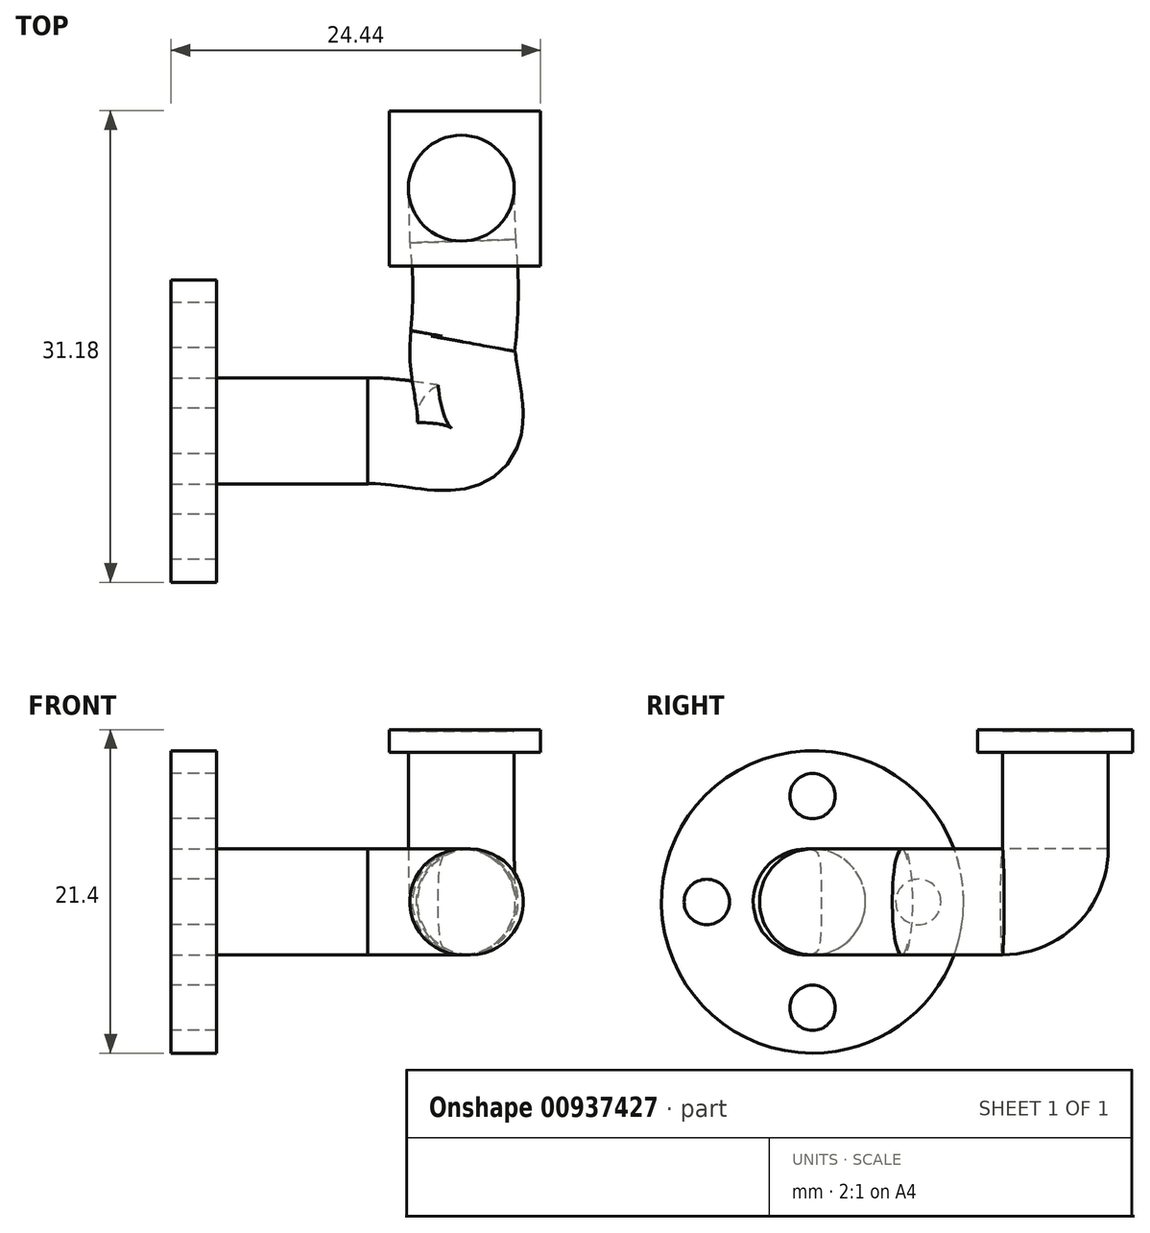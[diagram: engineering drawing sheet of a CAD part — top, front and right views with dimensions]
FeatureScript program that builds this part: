
annotation { "Feature Type Name" : "Feature", "Feature Type Description" : "" }
export const myFeature = defineFeature(function(context is Context, id is Id, definition is map)
    precondition{}
    {
        {
            var Q0;
            Q0=qCreatedBy(makeId("Right.planeOp"),FACE);
            var sketch = newSketch(context, id + "F0", { "sketchPlane" : qUnion([Q0])});
            skCircle(sketch, "E0", {"center": v(0, 7) * mm, "radius": 1.5 * mm});
            skCircle(sketch, "E1.1.0", {"center": v(-7, 0) * mm, "radius": 1.5 * mm});
            skCircle(sketch, "E1.2.0", {"center": v(0, -7) * mm, "radius": 1.5 * mm});
            skCircle(sketch, "E1.3.0", {"center": v(7, 0) * mm, "radius": 1.5 * mm});
            skPoint(sketch, "E1.center", {"position": v(0, 0) * mm});
            skCircle(sketch, "E2", {"center": v(0, 0) * mm, "radius": 10 * mm});
            skSolve(sketch);
        }
        {
            var Q0;
            Q0=qSketchRegion(id+"F0",true);
            extrude(context, id + "F1", {"entities" : qUnion([Q0]), "depth" : 3 * mm, "offsetDistance" : 25 * mm});
        }
        {
            var Q0;
            Q0=makeQuery(id+"F1.opExtrude","CAP_FACE",FACE,{"disambiguationData":[OSD([sQuery(id+"F0.wireOp",EDGE,"E0"),sQuery(id+"F0.wireOp",EDGE,"E1.1.0"),sQuery(id+"F0.wireOp",EDGE,"E1.2.0"),sQuery(id+"F0.wireOp",EDGE,"E1.3.0"),sQuery(id+"F0.wireOp",EDGE,"E2")])],"isStart":false});
            var sketch = newSketch(context, id + "F2", { "sketchPlane" : qUnion([Q0])});
            skCircle(sketch, "E3", {"center": v(0, 0) * mm, "radius": 3.5 * mm});
            skSolve(sketch);
        }
        {
            var Q0;
            Q0=qSketchRegion(id+"F2",true);
            extrude(context, id + "F3", {"entities" : qUnion([Q0]), "operationType" : NewBodyOperationType.ADD, "depth" : 10 * mm, "offsetDistance" : 25 * mm});
        }
        {
            var Q0;
            Q0=qSketchRegion(id+"F2",true);
            extrude(context, id + "F4", {"entities" : qUnion([Q0]), "operationType" : NewBodyOperationType.REMOVE, "endBound" : BoundingType.THROUGH_ALL, "oppositeDirection" : true, "depth" : 25 * mm, "offsetDistance" : 25 * mm});
        }
        {
            var Q0;
            Q0=qCreatedBy(makeId("Top.planeOp"),FACE);
            var sketch = newSketch(context, id + "F5", { "sketchPlane" : qUnion([Q0])});
            skFitSpline(sketch, "E4", {"points": [v(13.48, 0) * mm, v(19.49, 0) * mm, v(19.39, 6.5) * mm], "startDerivative": vector(13.33, 0) * mm, "endDerivative": vector(2.61, 14.76) * mm});
            skSolve(sketch);
        }
        {
            var Q0;
            Q0=makeQuery(id+"F3.opExtrude","CAP_FACE",FACE,{"disambiguationData":[OSD([sQuery(id+"F2.wireOp",EDGE,"E3")])],"isStart":false});
            var Q1;
            Q1=sQuery(id+"F5.wireOp",EDGE,"E4");
            sweep(context, id + "F6", {"operationType" : NewBodyOperationType.ADD, "profiles" : qUnion([Q0]), "path" : qUnion([Q1])});
        }
        {
            var Q0;
            Q0=qCreatedBy(makeId("Top.planeOp"),FACE);
            var sketch = newSketch(context, id + "F7", { "sketchPlane" : qUnion([Q0])});
            skArc(sketch, "E5", {"start": v(19.64, 5.83) * mm, "mid": v(19.83, 9.2) * mm, "end": v(19.67, 12.57) * mm});
            skSolve(sketch);
        }
        {
            var Q0;
            Q0=makeQuery(id+"F6.opSweep","CAP_FACE",FACE,{"disambiguationData":[OSD([sQuery(id+"F2.wireOp",EDGE,"E3"),sQuery(id+"F5.wireOp",VERTEX,"E4.end")])],"isStart":false});
            var Q1;
            Q1=sQuery(id+"F7.wireOp",EDGE,"E5");
            sweep(context, id + "F8", {"operationType" : NewBodyOperationType.ADD, "profiles" : qUnion([Q0]), "path" : qUnion([Q1])});
        }
        {
            var Q0;
            Q0=qCreatedBy(makeId("Top.planeOp"),FACE);
            cPlane(context, id + "F9", {"entities" : qUnion([Q0]), "cplaneType" : CPlaneType.OFFSET, "offset" : 3.5 * mm, "width" : 150 * mm, "height" : 150 * mm});
        }
        {
            var Q0;
            Q0=qCreatedBy(id+"F9.planeOp",FACE);
            var sketch = newSketch(context, id + "F10", { "sketchPlane" : qUnion([Q0])});
            skLineSegment(sketch, "E6.0", {"start": v(15.81, 12.45) * mm, "end": v(22.81, 12.67) * mm});
            skSolve(sketch);
        }
        {
            var Q0;
            Q0=makeQuery(id+"F8.opSweep","CAP_FACE",FACE,{"disambiguationData":[OSD([sQuery(id+"F2.wireOp",EDGE,"E3"),sQuery(id+"F5.wireOp",VERTEX,"E4.end"),sQuery(id+"F7.wireOp",VERTEX,"E5.end")])],"isStart":false});
            var Q1;
            Q1=sQuery(id+"F10.wireOp",EDGE,"E6.0");
            revolve(context, id + "F11", {"operationType" : NewBodyOperationType.ADD, "surfaceOperationType" : NewSurfaceOperationType.NEW, "entities" : qUnion([Q0]), "axis" : qUnion([Q1]), "revolveType" : RevolveType.ONE_DIRECTION, "angle" : 90 * degree});
        }
        {
            var Q0;
            Q0=makeQuery(id+"F11.opRevolve","CAP_FACE",FACE,{"disambiguationData":[OSD([sQuery(id+"F2.wireOp",EDGE,"E3"),sQuery(id+"F5.wireOp",VERTEX,"E4.end"),sQuery(id+"F7.wireOp",VERTEX,"E5.end")])],"isStart":false});
            extrude(context, id + "F12", {"entities" : qUnion([Q0]), "operationType" : NewBodyOperationType.ADD, "depth" : 6.4 * mm, "offsetDistance" : 25 * mm});
        }
        {
            var Q0;
            Q0=makeQuery(id+"F12.opExtrude","CAP_FACE",FACE,{"disambiguationData":[OSD([sQuery(id+"F2.wireOp",EDGE,"E3"),sQuery(id+"F5.wireOp",VERTEX,"E4.end"),sQuery(id+"F7.wireOp",VERTEX,"E5.end")])],"isStart":false});
            var sketch = newSketch(context, id + "F13", { "sketchPlane" : qUnion([Q0])});
            skLineSegment(sketch, "E7.bottom", {"start": v(24.44, 21.18) * mm, "end": v(14.44, 21.18) * mm});
            skLineSegment(sketch, "E7.top", {"start": v(24.44, 10.92) * mm, "end": v(14.44, 10.92) * mm});
            skLineSegment(sketch, "E7.left", {"start": v(24.44, 21.18) * mm, "end": v(24.44, 10.92) * mm});
            skLineSegment(sketch, "E7.right", {"start": v(14.44, 21.18) * mm, "end": v(14.44, 10.92) * mm});
            skSolve(sketch);
        }
        {
            var Q0;
            Q0=makeQuery(id+"F13.imprint","IMPRINT",FACE,{"disambiguationData":[TD([[makeQuery(id+"F13.imprint","IMPRINT",EDGE,{"derivedFrom":sQuery(id+"F13.wireOp",EDGE,"E7.bottom")}),1.0]])]});
            extrude(context, id + "F14", {"entities" : qUnion([Q0]), "operationType" : NewBodyOperationType.ADD, "depth" : 1.5 * mm, "offsetDistance" : 25 * mm});
        }
        {
            var Q0;
            Q0=makeQuery(id+"F12.opExtrude","CAP_FACE",FACE,{"disambiguationData":[OSD([sQuery(id+"F2.wireOp",EDGE,"E3"),sQuery(id+"F5.wireOp",VERTEX,"E4.end"),sQuery(id+"F7.wireOp",VERTEX,"E5.end")])],"isStart":false});
            extrude(context, id + "F15", {"entities" : qUnion([Q0]), "depth" : 1.4 * mm, "offsetDistance" : 25 * mm});
        }
        {
            var Q0;
            Q0=makeQuery(id+"F4.boolean.opBoolean","SPLIT",BODY,{"disambiguationData":[OD(0.0)],"derivedFrom":makeQuery(id+"F1.opExtrude","SWEPT_BODY",BODY,{"disambiguationData":[OSD([sQuery(id+"F0.wireOp",EDGE,"E0"),sQuery(id+"F0.wireOp",EDGE,"E1.1.0"),sQuery(id+"F0.wireOp",EDGE,"E1.2.0"),sQuery(id+"F0.wireOp",EDGE,"E1.3.0"),sQuery(id+"F0.wireOp",EDGE,"E2")])]})});
            var Q1;
            Q1=makeQuery(id+"F4.boolean.opBoolean","SPLIT",BODY,{"disambiguationData":[OD(1.0)],"derivedFrom":makeQuery(id+"F1.opExtrude","SWEPT_BODY",BODY,{"disambiguationData":[OSD([sQuery(id+"F0.wireOp",EDGE,"E0"),sQuery(id+"F0.wireOp",EDGE,"E1.1.0"),sQuery(id+"F0.wireOp",EDGE,"E1.2.0"),sQuery(id+"F0.wireOp",EDGE,"E1.3.0"),sQuery(id+"F0.wireOp",EDGE,"E2")])]})});
            var Q2;
            Q2=makeQuery(id+"F14.opExtrude","SWEPT_BODY",BODY,{"disambiguationData":[OSD([sQuery(id+"F2.wireOp",EDGE,"E3"),sQuery(id+"F5.wireOp",VERTEX,"E4.end"),sQuery(id+"F7.wireOp",VERTEX,"E5.end"),sQuery(id+"F13.wireOp",EDGE,"E7.bottom"),sQuery(id+"F13.wireOp",EDGE,"E7.top"),sQuery(id+"F13.wireOp",EDGE,"E7.left"),sQuery(id+"F13.wireOp",EDGE,"E7.right")])]});
            var Q3;
            Q3=makeQuery(id+"F15.opExtrude","SWEPT_BODY",BODY,{"disambiguationData":[OSD([sQuery(id+"F2.wireOp",EDGE,"E3"),sQuery(id+"F5.wireOp",VERTEX,"E4.end"),sQuery(id+"F7.wireOp",VERTEX,"E5.end")])]});
            booleanBodies(context, id + "F16", {"operationType" : BooleanOperationType.UNION, "tools" : qUnion([Q0, Q1, Q2, Q3])});
        }
    });
